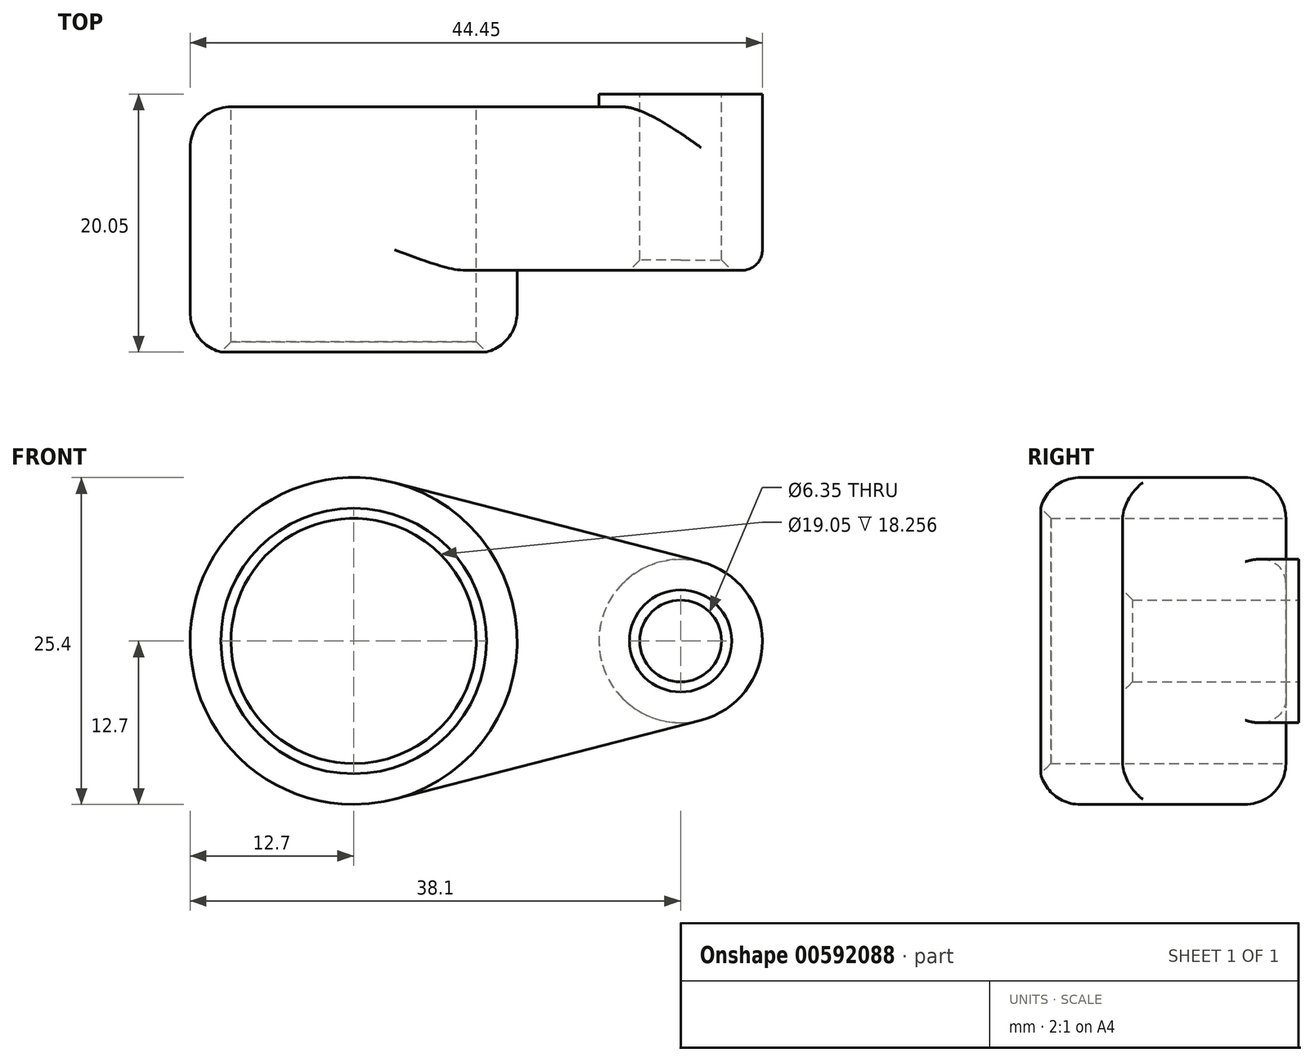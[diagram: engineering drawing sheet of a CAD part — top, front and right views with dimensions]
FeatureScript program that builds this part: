
annotation { "Feature Type Name" : "Feature", "Feature Type Description" : "" }
export const myFeature = defineFeature(function(context is Context, id is Id, definition is map)
    precondition{}
    {
        {
            var Q0;
            Q0=qCreatedBy(makeId("Front.planeOp"),FACE);
            var sketch = newSketch(context, id + "F0", { "sketchPlane" : qUnion([Q0])});
            skCircle(sketch, "E0", {"center": v(25.4, 0) * mm, "radius": 6.35 * mm});
            skLineSegment(sketch, "E1", {"start": v(3.17, 12.3) * mm, "end": v(26.99, 6.15) * mm});
            skLineSegment(sketch, "E2", {"start": v(3.17, -12.3) * mm, "end": v(26.99, -6.15) * mm});
            skCircle(sketch, "E3.0", {"center": v(0, 0) * mm, "radius": 9.53 * mm});
            skCircle(sketch, "E4.0", {"center": v(25.4, 0) * mm, "radius": 3.18 * mm});
            skArc(sketch, "E5", {"start": v(3.17, 12.3) * mm, "mid": v(-12.7, 0) * mm, "end": v(3.17, -12.3) * mm});
            skArc(sketch, "E6", {"start": v(3.17, -12.3) * mm, "mid": v(12.7, 0) * mm, "end": v(3.18, 12.3) * mm});
            skSolve(sketch);
        }
        {
            var Q0;
            Q0=makeQuery(id+"F0.imprint","IMPRINT",FACE,{"disambiguationData":[TD([[makeQuery(id+"F0.imprint","IMPRINT",EDGE,{"derivedFrom":sQuery(id+"F0.wireOp",EDGE,"E4.0")}),-1.0]])]});
            var Q1;
            Q1 = qSketchRegion(id + "F0", true);
            var Q2;
            {var subQ0=sQuery(id+"F0.wireOp",EDGE,"E1");Q2=makeQuery(id+"F0.imprint","IMPRINT",FACE,{"disambiguationData":[TD([[makeQuery(id+"F0.imprint","IMPRINT",EDGE,{"derivedFrom":subQ0}),-1.0]])]});}
            var Q3;
            Q3=makeQuery(id+"F0.imprint","IMPRINT",FACE,{"disambiguationData":[TD([[makeQuery(id+"F0.imprint","IMPRINT",EDGE,{"derivedFrom":sQuery(id+"F0.wireOp",EDGE,"E3.0")}),-1.0]])]});
            extrude(context, id + "F1", {"entities" : qUnion([Q0, Q1, Q2, Q3]), "depth" : 12.7 * mm, "offsetDistance" : 25.4 * mm});
        }
        {
            var Q0;
            Q0=makeQuery(id+"F0.imprint","IMPRINT",FACE,{"disambiguationData":[TD([[makeQuery(id+"F0.imprint","IMPRINT",EDGE,{"derivedFrom":sQuery(id+"F0.wireOp",EDGE,"E3.0")}),-1.0]])]});
            extrude(context, id + "F2", {"entities" : qUnion([Q0]), "operationType" : NewBodyOperationType.ADD, "depth" : 19.05 * mm, "offsetDistance" : 25.4 * mm});
        }
        {
            var Q0;
            Q0=makeQuery(id+"F2.opExtrude","CAP_EDGE",EDGE,{"disambiguationData":[OSD([sQuery(id+"F0.wireOp",EDGE,"eae8da73-eefe-4fc5-9817-fa2951d65bbc")])],"isStart":false});
            var Q1;
            Q1=makeQuery(id+"F1.opExtrude","CAP_EDGE",EDGE,{"disambiguationData":[OSD([sQuery(id+"F0.wireOp",EDGE,"E1")])],"isStart":false});
            fillet(context, id + "F3", {"entities" : qUnion([Q0, Q1]), "radius" : 1.59 * mm, "tangentPropagation" : true, "allowEdgeOverflow" : false});
        }
        {
            var Q0;
            Q0=makeQuery(id+"F2.opExtrude","CAP_EDGE",EDGE,{"disambiguationData":[OSD([sQuery(id+"F0.wireOp",EDGE,"E3.0")])],"isStart":false});
            var Q1;
            Q1=makeQuery(id+"F1.opExtrude","CAP_EDGE",EDGE,{"disambiguationData":[OSD([sQuery(id+"F0.wireOp",EDGE,"E4.0")])],"isStart":false});
            chamfer(context, id + "F4", {"entities" : qUnion([Q0, Q1]), "width" : 0.8 * mm, "tangentPropagation" : true});
        }
        {
            var Q0;
            Q0=makeQuery(id+"F0.imprint","IMPRINT",FACE,{"disambiguationData":[TD([[makeQuery(id+"F0.imprint","IMPRINT",EDGE,{"derivedFrom":sQuery(id+"F0.wireOp",EDGE,"E4.0")}),-1.0]])]});
            extrude(context, id + "F5", {"entities" : qUnion([Q0]), "operationType" : NewBodyOperationType.ADD, "oppositeDirection" : true, "depth" : 6.35 * mm, "offsetDistance" : 25.4 * mm});
        }
        {
            var Q0;
            Q0=makeQuery(id+"F5.opExtrude","CAP_EDGE",EDGE,{"disambiguationData":[OSD([sQuery(id+"F0.wireOp",EDGE,"E0")])],"isStart":false});
            fillet(context, id + "F6", {"entities" : qUnion([Q0]), "radius" : 6.1 * mm, "tangentPropagation" : true, "allowEdgeOverflow" : false});
        }
        {
            var Q0;
            {var subQ0=sQuery(id+"F0.wireOp",EDGE,"E4.0");Q0=makeQuery(id+"F6.opFillet","BLEND_EDGE",EDGE,{"blendedFrom":[makeQuery(id+"F5.opExtrude","CAP_EDGE",EDGE,{"disambiguationData":[OSD([sQuery(id+"F0.wireOp",EDGE,"E0")])],"isStart":false}),makeQuery(id+"F5.boolean.opBoolean","MERGE",FACE,{"derivedFrom":[makeQuery(id+"F1.opExtrude","SWEPT_FACE",FACE,{"disambiguationData":[OSD([subQ0])]}),makeQuery(id+"F5.opExtrude","SWEPT_FACE",FACE,{"disambiguationData":[OSD([subQ0])]})]})],"blendedInto":[makeQuery(id+"F5.boolean.opBoolean","MERGE",FACE,{"derivedFrom":[makeQuery(id+"F1.opExtrude","SWEPT_FACE",FACE,{"disambiguationData":[OSD([subQ0])]}),makeQuery(id+"F5.opExtrude","SWEPT_FACE",FACE,{"disambiguationData":[OSD([subQ0])]})]})]});}
            chamfer(context, id + "F7", {"entities" : qUnion([Q0]), "width" : 1.59 * mm, "tangentPropagation" : true});
        }
        {
            var Q0;
            Q0=makeQuery(id+"F1.opExtrude","CAP_EDGE",EDGE,{"disambiguationData":[OSD([sQuery(id+"F0.wireOp",EDGE,"E1")])],"isStart":true});
            var Q1;
            Q1=makeQuery(id+"F1.opExtrude","CAP_EDGE",EDGE,{"disambiguationData":[OSD([sQuery(id+"F0.wireOp",EDGE,"E5")])],"isStart":true});
            var Q2;
            Q2=makeQuery(id+"F1.opExtrude","CAP_EDGE",EDGE,{"disambiguationData":[OSD([sQuery(id+"F0.wireOp",EDGE,"E2")])],"isStart":true});
            fillet(context, id + "F8", {"entities" : qUnion([Q0, Q1, Q2]), "radius" : 3.17 * mm, "tangentPropagation" : true, "allowEdgeOverflow" : false});
        }
        {
            var Q0;
            Q0=makeQuery(id+"F2.opExtrude","CAP_EDGE",EDGE,{"disambiguationData":[OSD([sQuery(id+"F0.wireOp",EDGE,"E5"),sQuery(id+"F0.wireOp",EDGE,"E6")])],"isStart":false});
            fillet(context, id + "F9", {"entities" : qUnion([Q0]), "radius" : 3.17 * mm, "tangentPropagation" : true, "allowEdgeOverflow" : false});
        }
    });
